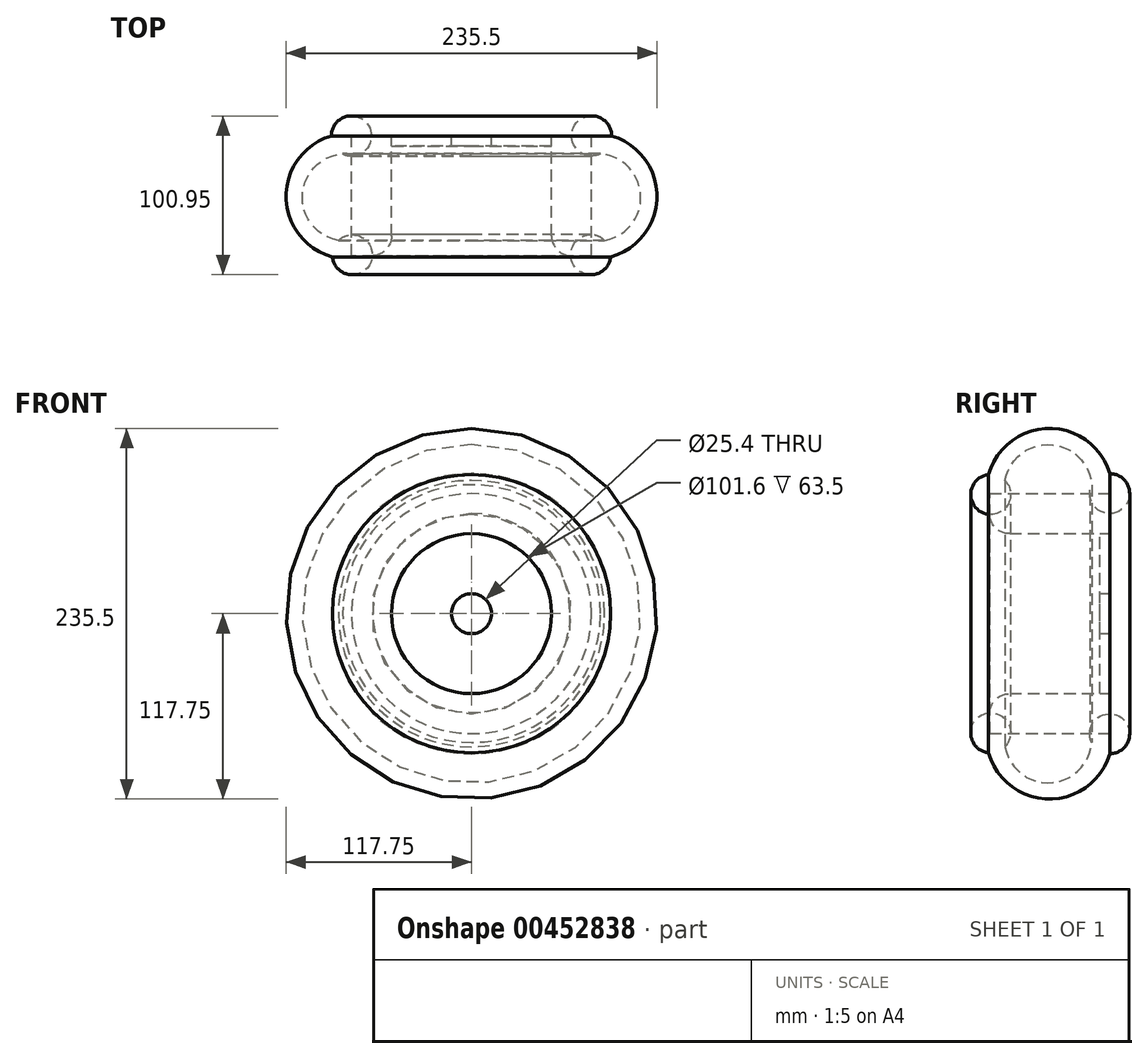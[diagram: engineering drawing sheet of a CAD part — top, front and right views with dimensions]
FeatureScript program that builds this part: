
annotation { "Feature Type Name" : "Feature", "Feature Type Description" : "" }
export const myFeature = defineFeature(function(context is Context, id is Id, definition is map)
    precondition{}
    {
        {
            var Q0;
            Q0=qCreatedBy(makeId("Front.planeOp"),FACE);
            var sketch = newSketch(context, id + "F0", { "sketchPlane" : qUnion([Q0])});
            skCircle(sketch, "E0", {"center": v(0, 0) * mm, "radius": 76.2 * mm});
            skLineSegment(sketch, "E1", {"start": v(-84.3, -59.56) * mm, "end": v(-84.3, 78.72) * mm, "construction": true});
            skCircle(sketch, "E2", {"center": v(0, 0) * mm, "radius": 50.8 * mm});
            skSolve(sketch);
        }
        {
            var Q0;
            Q0 = qSketchRegion(id + "F0", true);
            extrude(context, id + "F1", {"entities" : qUnion([Q0]), "depth" : 76.2 * mm});
        }
        {
            var Q0;
            Q0=qCreatedBy(makeId("Right.planeOp"),FACE);
            var sketch = newSketch(context, id + "F2", { "sketchPlane" : qUnion([Q0])});
            skCircle(sketch, "E3", {"center": v(-75.55, 75.72) * mm, "radius": 12.7 * mm});
            skCircle(sketch, "E4", {"center": v(0, 76.3) * mm, "radius": 12.7 * mm});
            skArc(sketch, "E5", {"start": v(0, 89) * mm, "mid": v(-38.7, 117.75) * mm, "end": v(-76.9, 88.35) * mm});
            skArc(sketch, "E6", {"start": v(-11.4, 81.88) * mm, "mid": v(-37.74, 107.43) * mm, "end": v(-66.45, 84.58) * mm});
            skSolve(sketch);
        }
        {
            var Q0;
            Q0=qCreatedBy(makeId("Right.planeOp"),FACE);
            var sketch = newSketch(context, id + "F3", { "sketchPlane" : qUnion([Q0])});
            skLineSegment(sketch, "E7", {"start": v(0, 0) * mm, "end": v(-50.56, 0) * mm, "construction": true});
            skSolve(sketch);
        }
        {
            var Q0;
            Q0 = qSketchRegion(id + "F2", true);
            var Q1;
            Q1=sQuery(id+"F3.wireOp",EDGE,"E7");
            revolve(context, id + "F4", {"entities" : qUnion([Q0]), "axis" : qUnion([Q1]), "revolveType" : RevolveType.FULL});
        }
        {
            var Q0;
            Q0=qCreatedBy(makeId("Front.planeOp"),FACE);
            var sketch = newSketch(context, id + "F5", { "sketchPlane" : qUnion([Q0])});
            skCircle(sketch, "E8", {"center": v(0, 0) * mm, "radius": 50.8 * mm});
            skSolve(sketch);
        }
        {
            var Q0;
            Q0 = qSketchRegion(id + "F5", true);
            extrude(context, id + "F6", {"entities" : qUnion([Q0]), "depth" : 6.35 * mm});
        }
        {
            var Q0;
            Q0=makeQuery(id+"F1.opExtrude","CAP_EDGE",EDGE,{"disambiguationData":[OSD([sQuery(id+"F0.wireOp",EDGE,"E2")])],"isStart":false});
            fillet(context, id + "F7", {"entities" : qUnion([Q0]), "radius" : 12.7 * mm, "tangentPropagation" : true, "allowEdgeOverflow" : false});
        }
        {
            var Q0;
            Q0=sQuery(id+"F0.wireOp",VERTEX,"E2.center");
            var Q1;
            Q1=makeQuery(id+"F6.opExtrude","SWEPT_BODY",BODY,{"disambiguationData":[OSD([sQuery(id+"F5.wireOp",EDGE,"E8")])]});
            hole(context, id + "F8", {"style" : HoleStyle.SIMPLE, "endStyle" : HoleEndStyle.BLIND, "oppositeDirection" : true, "holeDiameter" : 25.4 * mm, "holeDepth" : 12.7 * mm, "isTappedThrough" : true, "tappedDepth" : 12.7 * mm, "tapClearance" : 3, "locations" : qUnion([Q0]), "scope" : qUnion([Q1])});
        }
    });
